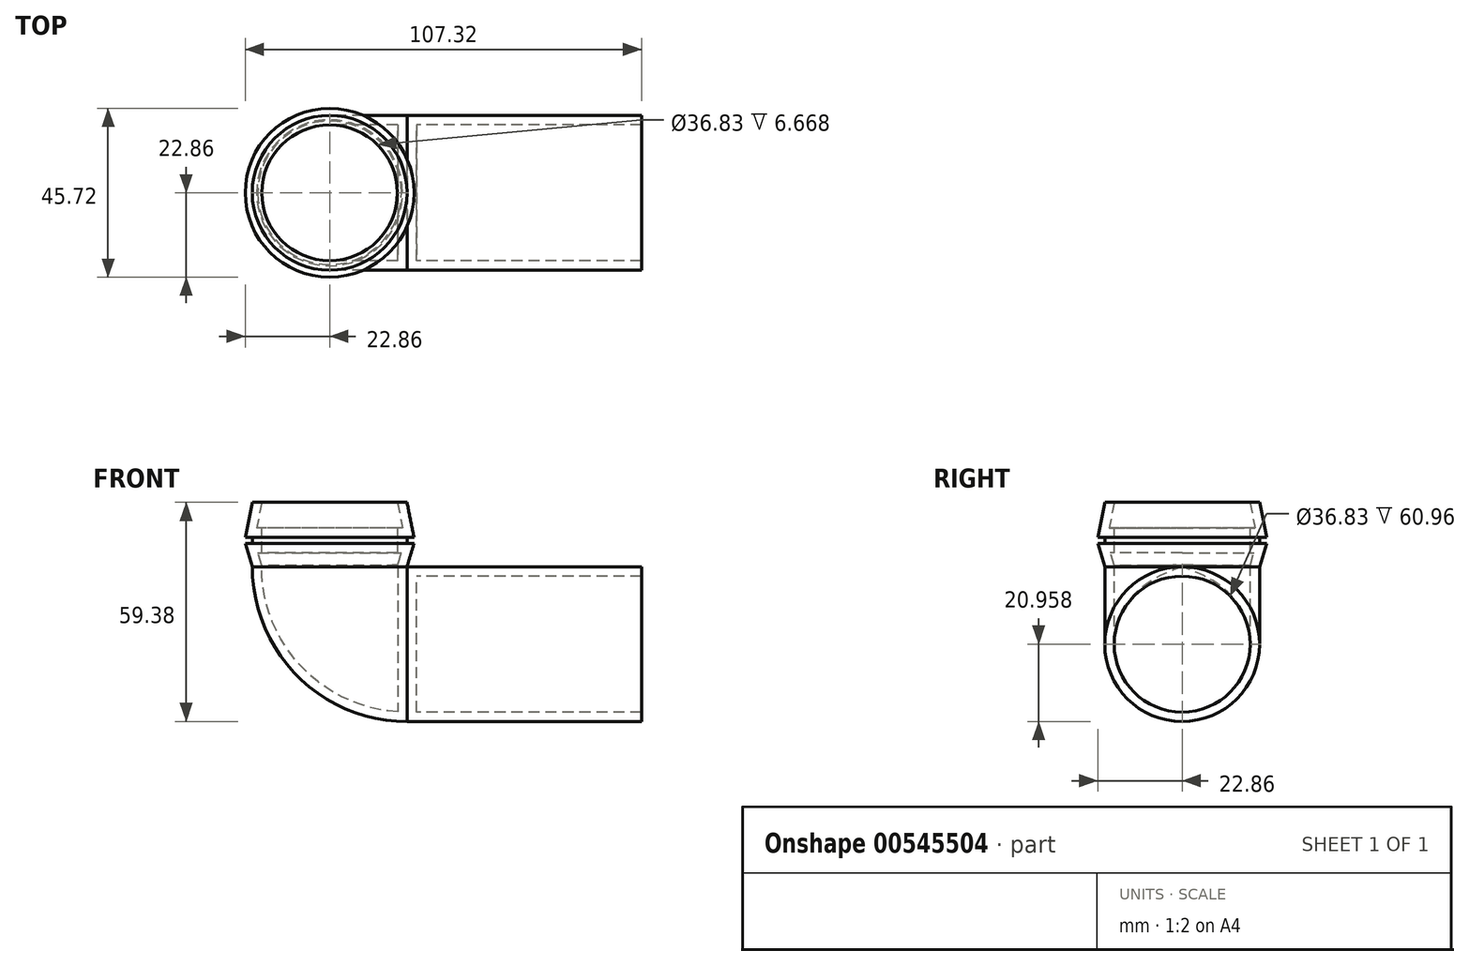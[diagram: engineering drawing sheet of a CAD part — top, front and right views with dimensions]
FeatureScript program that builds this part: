
annotation { "Feature Type Name" : "Feature", "Feature Type Description" : "" }
export const myFeature = defineFeature(function(context is Context, id is Id, definition is map)
    precondition{}
    {
        {
            var Q0;
            Q0=qCreatedBy(makeId("Top.planeOp"),FACE);
            var sketch = newSketch(context, id + "F0", { "sketchPlane" : qUnion([Q0])});
            skCircle(sketch, "E0", {"center": v(0, 0) * mm, "radius": 22.86 * mm});
            skSolve(sketch);
        }
        {
            var Q0;
            Q0=qCreatedBy(makeId("Top.planeOp"),FACE);
            cPlane(context, id + "F1", {"entities" : qUnion([Q0]), "cplaneType" : CPlaneType.OFFSET, "offset" : 9.52 * mm, "width" : 152.4 * mm, "height" : 152.4 * mm});
        }
        {
            var Q0;
            Q0=qCreatedBy(id+"F1.planeOp",FACE);
            var sketch = newSketch(context, id + "F2", { "sketchPlane" : qUnion([Q0])});
            skCircle(sketch, "E1", {"center": v(0, 0) * mm, "radius": 20.96 * mm});
            skSolve(sketch);
        }
        {
            var Q0;
            Q0=makeQuery(id+"F2.imprint","IMPRINT",FACE,{"disambiguationData":[TD([[makeQuery(id+"F2.imprint","IMPRINT",EDGE,{"derivedFrom":sQuery(id+"F2.wireOp",EDGE,"E1")}),1.0]])]});
            var Q1;
            Q1=makeQuery(id+"F0.imprint","IMPRINT",FACE,{"disambiguationData":[TD([[makeQuery(id+"F0.imprint","IMPRINT",EDGE,{"derivedFrom":sQuery(id+"F0.wireOp",EDGE,"E0")}),1.0]])]});
            loft(context, id + "F3", {"sheetProfilesArray" : [{ "sheetProfileEntities" : qUnion([Q0]) }, { "sheetProfileEntities" : qUnion([Q1]) }]});
        }
        {
            var Q0;
            Q0=qCreatedBy(makeId("Top.planeOp"),FACE);
            var sketch = newSketch(context, id + "F4", { "sketchPlane" : qUnion([Q0])});
            skCircle(sketch, "E2", {"center": v(0, 0) * mm, "radius": 20.96 * mm});
            skSolve(sketch);
        }
        {
            var Q0;
            Q0=qSketchRegion(id+"F4",true);
            extrude(context, id + "F5", {"entities" : qUnion([Q0]), "operationType" : NewBodyOperationType.ADD, "oppositeDirection" : true, "depth" : 1.59 * mm, "offsetDistance" : 25.4 * mm});
        }
        {
            var Q0;
            Q0=makeQuery(id+"F5.opExtrude","CAP_FACE",FACE,{"disambiguationData":[OSD([sQuery(id+"F4.wireOp",EDGE,"E2")])],"isStart":false});
            cPlane(context, id + "F6", {"entities" : qUnion([Q0]), "cplaneType" : CPlaneType.OFFSET, "offset" : 0 * mm, "width" : 152.4 * mm, "height" : 152.4 * mm});
        }
        {
            var Q0;
            Q0=qCreatedBy(id+"F6.planeOp",FACE);
            var sketch = newSketch(context, id + "F7", { "sketchPlane" : qUnion([Q0])});
            skCircle(sketch, "E3", {"center": v(0, 0) * mm, "radius": 22.86 * mm});
            skSolve(sketch);
        }
        {
            var Q0;
            Q0=qCreatedBy(id+"F6.planeOp",FACE);
            var Q1;
            Q1=qBodyType(qCreatedBy(id+"F9",EDGE),BodyType.WIRE);
            cPlane(context, id + "F8", {"entities" : qUnion([Q0, Q1]), "cplaneType" : CPlaneType.OFFSET, "offset" : 6.35 * mm, "width" : 152.4 * mm, "height" : 152.4 * mm});
        }
        {
            var Q0;
            Q0=qCreatedBy(id+"F8.planeOp",FACE);
            var sketch = newSketch(context, id + "F9", { "sketchPlane" : qUnion([Q0])});
            skCircle(sketch, "E4", {"center": v(0, 0) * mm, "radius": 20.96 * mm});
            skLineSegment(sketch, "E5", {"start": v(20.96, 0) * mm, "end": v(20.96, -56.5) * mm, "construction": true});
            skLineSegment(sketch, "E6", {"start": v(20.96, -56.5) * mm, "end": v(20.96, 40.67) * mm, "construction": true});
            skSolve(sketch);
        }
        {
            var Q1;
            Q1=makeQuery(id+"F9.imprint","IMPRINT",FACE,{"disambiguationData":[TD([[makeQuery(id+"F9.imprint","IMPRINT",EDGE,{"derivedFrom":sQuery(id+"F9.wireOp",EDGE,"E4")}),1.0]])]});
            var Q2;
            Q2=makeQuery(id+"F7.imprint","IMPRINT",FACE,{"disambiguationData":[TD([[makeQuery(id+"F7.imprint","IMPRINT",EDGE,{"derivedFrom":sQuery(id+"F7.wireOp",EDGE,"E3")}),1.0]])]});
            loft(context, id + "F10", {"operationType" : NewBodyOperationType.ADD, "sheetProfilesArray" : [{ "sheetProfileEntities" : qUnion([Q1]) }, { "sheetProfileEntities" : qUnion([Q2]) }]});
        }
        {
            var Q0;
            Q0=makeQuery(id+"F9.imprint","IMPRINT",FACE,{"disambiguationData":[TD([[makeQuery(id+"F9.imprint","IMPRINT",EDGE,{"derivedFrom":sQuery(id+"F9.wireOp",EDGE,"E4")}),1.0]])]});
            var Q1;
            Q1=sQuery(id+"F9.wireOp",EDGE,"E6");
            revolve(context, id + "F11", {"operationType" : NewBodyOperationType.ADD, "entities" : qUnion([Q0]), "axis" : qUnion([Q1]), "revolveType" : RevolveType.ONE_DIRECTION, "angle" : 90 * degree});
        }
        {
            var Q0;
            Q0=makeQuery(id+"F11.opRevolve","CAP_FACE",FACE,{"disambiguationData":[OSD([sQuery(id+"F9.wireOp",EDGE,"E4")])],"isStart":false});
            cPlane(context, id + "F12", {"entities" : qUnion([Q0]), "cplaneType" : CPlaneType.OFFSET, "offset" : 0 * mm, "width" : 152.4 * mm, "height" : 152.4 * mm});
        }
        {
            var Q0;
            Q0=makeQuery(id+"F11.opRevolve","CAP_FACE",FACE,{"disambiguationData":[OSD([sQuery(id+"F9.wireOp",EDGE,"E4")])],"isStart":false});
            extrude(context, id + "F13", {"entities" : qUnion([Q0]), "depth" : 63.5 * mm, "offsetDistance" : 25.4 * mm});
        }
        {
            var Q0;
            Q0=makeQuery(id+"F3.opLoft","CAP_FACE",FACE,{"disambiguationData":[OSD([makeQuery(id+"F2.imprint","IMPRINT",FACE,{"disambiguationData":[TD([[makeQuery(id+"F2.imprint","IMPRINT",EDGE,{"derivedFrom":sQuery(id+"F2.wireOp",EDGE,"E1")}),1.0]])]})])],"isStart":true});
            var Q1;
            Q1=makeQuery(id+"F13.opExtrude","CAP_FACE",FACE,{"disambiguationData":[OSD([sQuery(id+"F9.wireOp",EDGE,"E4")])],"isStart":false});
            shell(context, id + "F14", {"entities" : qUnion([Q0, Q1]), "thickness" : 2.54 * mm});
        }
    });
